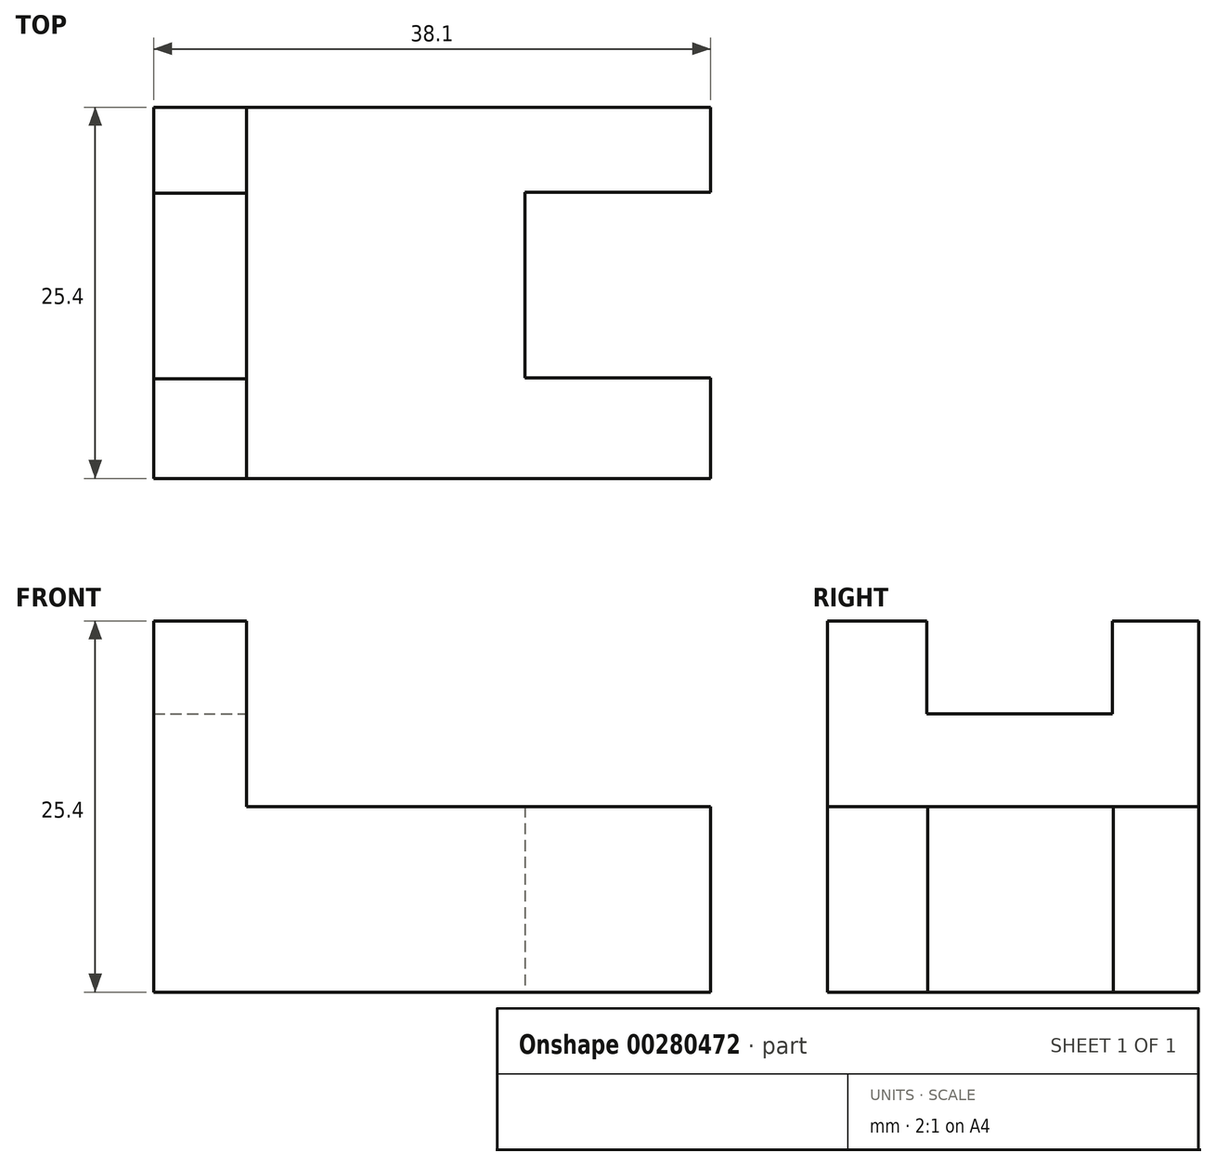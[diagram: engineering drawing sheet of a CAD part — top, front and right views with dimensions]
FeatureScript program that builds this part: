
annotation { "Feature Type Name" : "Feature", "Feature Type Description" : "" }
export const myFeature = defineFeature(function(context is Context, id is Id, definition is map)
    precondition{}
    {
        {
            var Q0;
            Q0=qCreatedBy(makeId("Front.planeOp"),FACE);
            var sketch = newSketch(context, id + "F0", { "sketchPlane" : qUnion([Q0])});
            skLineSegment(sketch, "E0", {"start": v(0, 0) * mm, "end": v(0, 25.4) * mm});
            skLineSegment(sketch, "E1", {"start": v(0, 25.4) * mm, "end": v(6.35, 25.4) * mm});
            skLineSegment(sketch, "E2", {"start": v(6.35, 25.4) * mm, "end": v(6.35, 12.7) * mm});
            skLineSegment(sketch, "E3", {"start": v(6.35, 12.7) * mm, "end": v(38.1, 12.7) * mm});
            skLineSegment(sketch, "E4", {"start": v(38.1, 12.7) * mm, "end": v(38.1, 0) * mm});
            skLineSegment(sketch, "E5", {"start": v(38.1, 0) * mm, "end": v(0, 0) * mm});
            skSolve(sketch);
        }
        {
            var Q0;
            Q0=makeQuery(id+"F0.imprint","IMPRINT",FACE,{"disambiguationData":[TD([[makeQuery(id+"F0.imprint","IMPRINT",EDGE,{"derivedFrom":sQuery(id+"F0.wireOp",EDGE,"E0")}),-1.0]])]});
            extrude(context, id + "F1", {"entities" : qUnion([Q0]), "depth" : 25.4 * mm});
        }
        {
            var Q0;
            Q0=makeQuery(id+"F1.opExtrude","SWEPT_FACE",FACE,{"disambiguationData":[OSD([sQuery(id+"F0.wireOp",EDGE,"E2")])]});
            var sketch = newSketch(context, id + "F2", { "sketchPlane" : qUnion([Q0])});
            skLineSegment(sketch, "E6", {"start": v(-18.6, 25.4) * mm, "end": v(-18.6, 19.05) * mm});
            skPoint(sketch, "E6.endSnap0", {"position": v(0, 19.05) * mm});
            skLineSegment(sketch, "E7", {"start": v(-18.6, 19.05) * mm, "end": v(-5.9, 19.05) * mm});
            skLineSegment(sketch, "E8", {"start": v(-5.9, 19.05) * mm, "end": v(-5.9, 25.4) * mm});
            skLineSegment(sketch, "E9", {"start": v(-5.9, 25.4) * mm, "end": v(-18.6, 25.4) * mm});
            skSolve(sketch);
        }
        {
            var Q0;
            Q0=makeQuery(id+"F2.imprint","IMPRINT",FACE,{"disambiguationData":[TD([[makeQuery(id+"F2.imprint","IMPRINT",EDGE,{"derivedFrom":sQuery(id+"F2.wireOp",EDGE,"E6")}),1.0]])]});
            extrude(context, id + "F3", {"entities" : qUnion([Q0]), "operationType" : NewBodyOperationType.REMOVE, "oppositeDirection" : true, "depth" : 6.35 * mm});
        }
        {
            var Q0;
            Q0=makeQuery(id+"F1.opExtrude","SWEPT_FACE",FACE,{"disambiguationData":[OSD([sQuery(id+"F0.wireOp",EDGE,"E4")])]});
            var sketch = newSketch(context, id + "F4", { "sketchPlane" : qUnion([Q0])});
            skLineSegment(sketch, "E10", {"start": v(-18.53, 12.7) * mm, "end": v(-18.53, 0) * mm});
            skLineSegment(sketch, "E11", {"start": v(-18.53, 0) * mm, "end": v(-5.83, 0) * mm});
            skLineSegment(sketch, "E12", {"start": v(-5.83, 0) * mm, "end": v(-5.83, 12.7) * mm});
            skLineSegment(sketch, "E13", {"start": v(-5.83, 12.7) * mm, "end": v(-18.53, 12.7) * mm});
            skSolve(sketch);
        }
        {
            var Q0;
            Q0=makeQuery(id+"F4.imprint","IMPRINT",FACE,{"disambiguationData":[TD([[makeQuery(id+"F4.imprint","IMPRINT",EDGE,{"derivedFrom":sQuery(id+"F4.wireOp",EDGE,"E10")}),1.0]])]});
            extrude(context, id + "F5", {"entities" : qUnion([Q0]), "operationType" : NewBodyOperationType.REMOVE, "oppositeDirection" : true, "depth" : 12.7 * mm});
        }
    });
